# Revit family: Bath-Alcove-Kohler-Mariposa-K_1259-A
name_source: partatom
category: Plumbing Fixtures
revit_build: Autodesk Revit 2015 (Build: 20140606_1530(x64)
units: mm (PartAtom-declared; Revit-internal decimal feet)

## types (10) — shared parameters
ADA Compliant = No
Assembly Code = D2010510
CW Connection = No
Default Elevation = 0' - 0"
Drain Diameter = 0' - 1 1/2"
HW Connection = No
Height = 1' - 9 1/4"
Keynote = 22 40 00.D2
Length = 6' - 0"
Manufacturer = Kohler
Material = Acrylic
Product Documentation Link = http://www.us.kohler.com
Product Name = Mariposa 72'' x 36'' Alcove Bath with Apron
Product Page URL = http://www.us.kohler.com
Sanitary Connector = Sanitary Drain
URL = http://www.us.kohler.com
Version = 2014 - v1.0a
Waste Connection = Yes
Water Capacity = 72 gal (272.5 L)
Weight = 77 lbs (34.9 kg)
Width = 3' - 0"
zero-valued in all types: CWFU, HWFU, WFU

## per-type parameters (varying)
| type | Constraint | ControlM | Description | Finish | Model | Vent Connection |
| Right Drain Apron, 0-White | 1 | 1425 | 72'' x 36'' Alcove Bath, Right Hand Drain with Flange and Apron, Dune | Acrylic - Kohler - NY - Dune | K-1259-RA-NY | Yes |
| Right Drain Apron, 47-Almond | 1 | 47 | 72'' x 36'' Alcove Bath, Right Hand Drain with Flange and Apron, Almond | Acrylic - Kohler - 47 - Almond | K-1259-RA-47 | Yes |
| Right Drain Apron, 96-Biscut | 1 | 96 | 72'' x 36'' Alcove Bath, Right Hand Drain with Flange and Apron, Biscuit | Acrylic - Kohler - 96 - Biscuit | K-1259-RA-96 | Yes |
| Right Drain Apron, G9-Sandbar | 1 | 79 | 72'' x 36'' Alcove Bath, Right Hand Drain with Flange and Apron, Sandbar | Acrylic - Kohler - G9 - Sandbar | K-1259-RA-G9 | Yes |
| Right Drain Apron, NY-Dune | 1 | 1425 | 72'' x 36'' Alcove Bath, Right Hand Drain with Flange and Apron, Dune | Acrylic - Kohler - NY - Dune | K-1259-RA-NY | Yes |
| Left Drain Apron, 0-White | 2 | 0 | 72'' x 36'' Alcove Bath, Left Hand Drain with Flange and Apron, White | Acrylic - Kohler - 0 - White | K-1259-LA-0 | No |
| Left Drain Apron, 47-Almond | 2 | 47 | 72'' x 36'' Alcove Bath, Left Hand Drain with Flange and Apron, Almond | Acrylic - Kohler - 47 - Almond | K-1259-LA-47 | Yes |
| Left Drain Apron, 96-Biscut | 2 | 96 | 72'' x 36'' Alcove Bath, Left Hand Drain with Flange and Apron, Biscuit | Acrylic - Kohler - 96 - Biscuit | K-1259-LA-96 | Yes |
| Left Drain Apron, G9-Sandbar | 2 | 79 | 72'' x 36'' Alcove Bath, Left Hand Drain with Flange and Apron, Sandbar | Acrylic - Kohler - G9 - Sandbar | K-1259-LA-G9 | Yes |
| Left Drain Apron, NY-Dune | 2 | 1425 | 72'' x 36'' Alcove Bath, Left Hand Drain with Flange and Apron, Dune | Acrylic - Kohler - NY - Dune | K-1259-LA-NY | Yes |

## geometry (parser evidence)
native form markers: Extrusion x5, Sweep x7
no freeform markers — native parametric forms only
